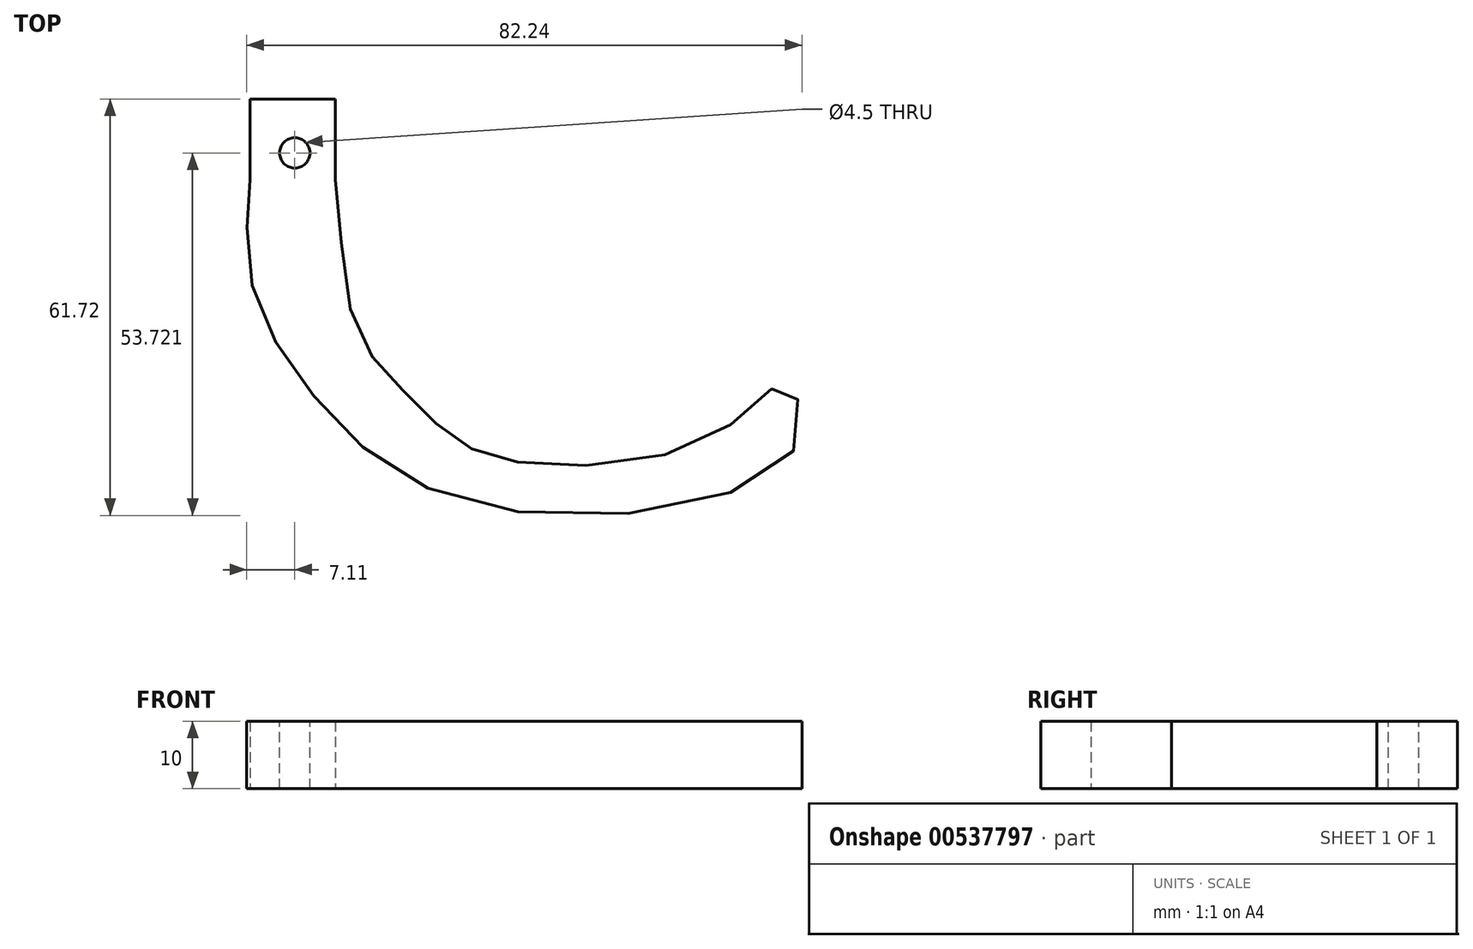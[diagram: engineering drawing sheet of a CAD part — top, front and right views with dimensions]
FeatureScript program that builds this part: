
annotation { "Feature Type Name" : "Feature", "Feature Type Description" : "" }
export const myFeature = defineFeature(function(context is Context, id is Id, definition is map)
    precondition{}
    {
        {
            var Q0;
            Q0=qCreatedBy(makeId("Top.planeOp"),FACE);
            var sketch = newSketch(context, id + "F0", { "sketchPlane" : qUnion([Q0])});
            skLineSegment(sketch, "E0.bottom", {"start": v(-24.97, 29.9) * mm, "end": v(-12.34, 29.9) * mm});
            skLineSegment(sketch, "E0.top", {"start": v(-24.97, 17.94) * mm, "end": v(-12.34, 17.94) * mm});
            skLineSegment(sketch, "E0.left", {"start": v(-24.97, 29.9) * mm, "end": v(-24.97, 17.94) * mm});
            skLineSegment(sketch, "E0.right", {"start": v(-12.34, 29.9) * mm, "end": v(-12.34, 17.94) * mm});
            skFitSpline(sketch, "E1", {"points": [v(-24.97, 17.94) * mm, v(-24.97, 3.61) * mm, v(-15.23, -14.49) * mm, v(10.7, -30.67) * mm, v(55.6, -22.14) * mm, v(54.38, -12.57) * mm, v(44.29, -19.7) * mm, v(16.17, -24.1) * mm, v(5.3, -20.4) * mm, v(-2.7, -12.92) * mm, v(-9.48, -3.35) * mm, v(-12.34, 17.94) * mm], "startDerivative": vector(-6.23, -128.4) * mm, "endDerivative": vector(-26.67, 181.33) * mm});
            skPoint(sketch, "E2.centerSnap0", {"position": v(-12.34, 23.92) * mm});
            skSolve(sketch);
        }
        {
            var Q0;
            Q0 = qSketchRegion(id + "F0", true);
            extrude(context, id + "F1", {"entities" : qUnion([Q0]), "depth" : 10 * mm, "offsetDistance" : 25 * mm});
        }
        {
            var Q0;
            Q0=makeQuery(id+"F1.opExtrude","CAP_FACE",FACE,{"disambiguationData":[OSD([sQuery(id+"F0.wireOp",EDGE,"E0.bottom"),sQuery(id+"F0.wireOp",EDGE,"E0.left"),sQuery(id+"F0.wireOp",EDGE,"E0.right"),sQuery(id+"F0.wireOp",EDGE,"E1"),sQuery(id+"F0.wireOp",EDGE,"E2")])],"isStart":false});
            var sketch = newSketch(context, id + "F2", { "sketchPlane" : qUnion([Q0])});
            skPoint(sketch, "E3", {"position": v(-18.34, 21.9) * mm});
            skSolve(sketch);
        }
        {
            var Q0;
            Q0=sQuery(id+"F2.wireOp",VERTEX,"E3");
            var Q1;
            Q1=makeQuery(id+"F1.opExtrude","SWEPT_BODY",BODY,{"disambiguationData":[OSD([sQuery(id+"F0.wireOp",EDGE,"E0.bottom"),sQuery(id+"F0.wireOp",EDGE,"E0.left"),sQuery(id+"F0.wireOp",EDGE,"E0.right"),sQuery(id+"F0.wireOp",EDGE,"E1"),sQuery(id+"F0.wireOp",EDGE,"E2")])]});
            hole(context, id + "F3", {"style" : HoleStyle.SIMPLE, "endStyle" : HoleEndStyle.THROUGH, "standardTappedOrClearance" : lookupTablePath({ "standard" : "ANSI", "fit" : "Normal (ASME)", "size" : "#8", "type" : "Clearance" }), "standardBlindInLast" : lookupTablePath({ "fit" : "Free", "standard" : "ANSI", "size" : "#8", "type" : "Clearance" }), "holeDiameter" : 4.5 * mm, "isTappedThrough" : true, "tappedDepth" : 12 * mm, "tapClearance" : 3, "locations" : qUnion([Q0]), "scope" : qUnion([Q1])});
        }
    });
